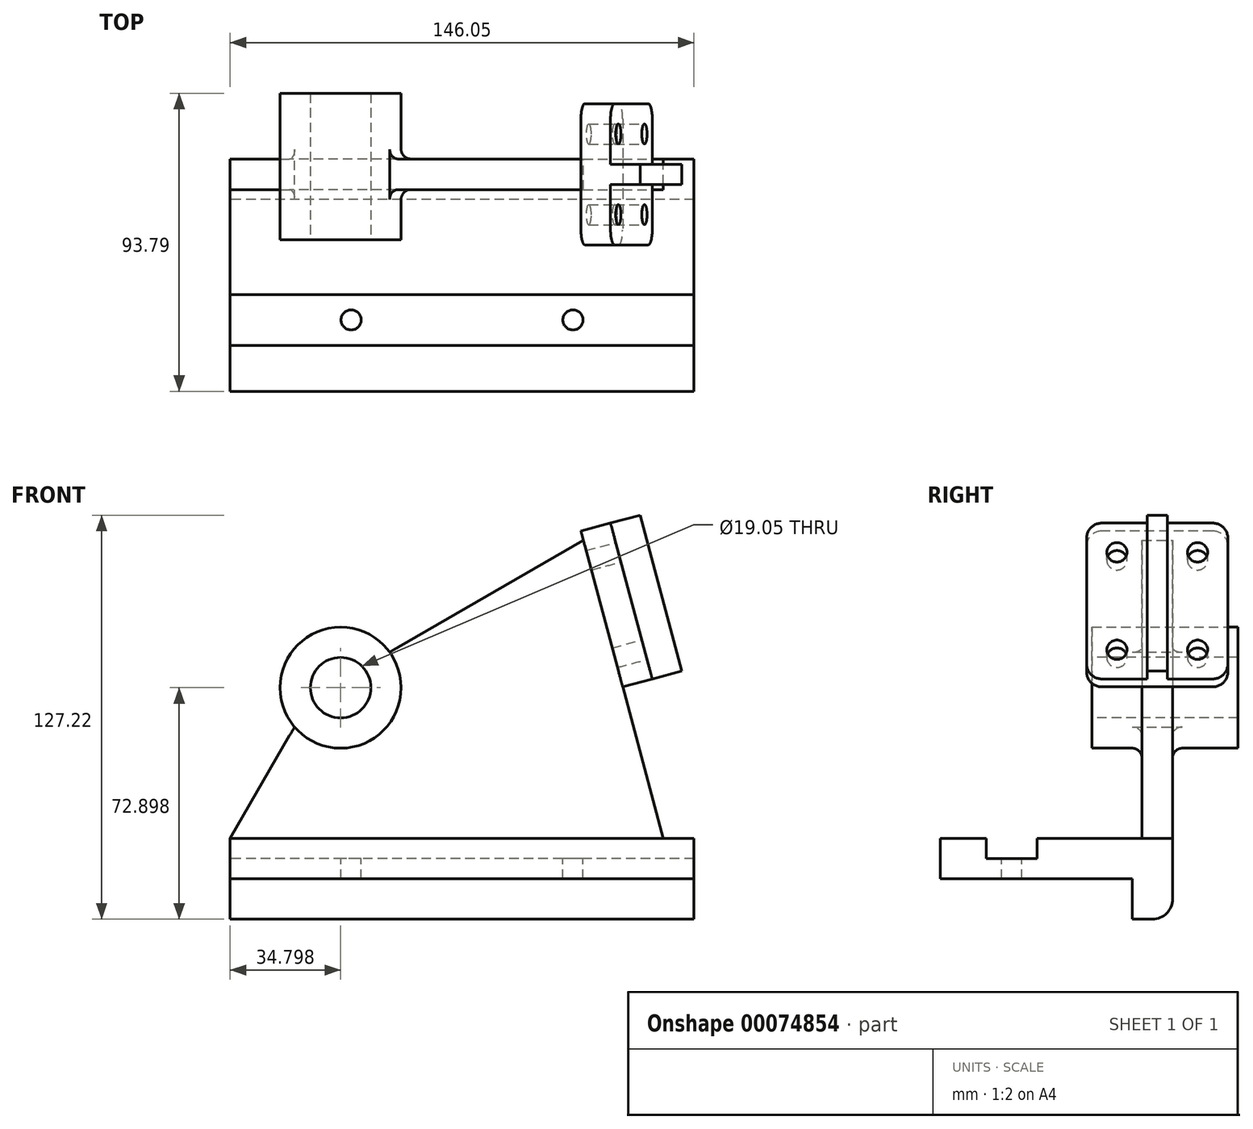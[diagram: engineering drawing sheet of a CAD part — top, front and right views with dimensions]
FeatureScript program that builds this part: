
annotation { "Feature Type Name" : "Feature", "Feature Type Description" : "" }
export const myFeature = defineFeature(function(context is Context, id is Id, definition is map)
    precondition{}
    {
        {
            var Q0;
            Q0=qCreatedBy(makeId("Right.planeOp"),FACE);
            var sketch = newSketch(context, id + "F0", { "sketchPlane" : qUnion([Q0])});
            skLineSegment(sketch, "E0", {"start": v(0, 0) * mm, "end": v(0, -25.4) * mm});
            skLineSegment(sketch, "E1", {"start": v(0, -25.4) * mm, "end": v(-12.7, -25.4) * mm});
            skLineSegment(sketch, "E2", {"start": v(-12.7, -25.4) * mm, "end": v(-12.7, -12.7) * mm});
            skLineSegment(sketch, "E3", {"start": v(-12.7, -12.7) * mm, "end": v(-73.15, -12.7) * mm});
            skLineSegment(sketch, "E4", {"start": v(-73.15, -12.7) * mm, "end": v(-73.15, 0) * mm});
            skLineSegment(sketch, "E5", {"start": v(-73.15, 0) * mm, "end": v(-58.67, 0) * mm});
            skLineSegment(sketch, "E6", {"start": v(-58.67, 0) * mm, "end": v(-58.67, -6.35) * mm});
            skLineSegment(sketch, "E7", {"start": v(-58.67, -6.35) * mm, "end": v(-42.67, -6.35) * mm});
            skLineSegment(sketch, "E8", {"start": v(-42.67, -6.35) * mm, "end": v(-42.67, 0) * mm});
            skLineSegment(sketch, "E9", {"start": v(-42.67, 0) * mm, "end": v(0, 0) * mm});
            skSolve(sketch);
        }
        {
            var Q0;
            Q0 = qSketchRegion(id + "F0", true);
            extrude(context, id + "F1", {"entities" : qUnion([Q0]), "depth" : 146.05 * mm});
        }
        {
            var Q0;
            Q0=makeQuery(id+"F1.opExtrude","SWEPT_FACE",FACE,{"disambiguationData":[OSD([sQuery(id+"F0.wireOp",EDGE,"E7")])]});
            var sketch = newSketch(context, id + "F2", { "sketchPlane" : qUnion([Q0])});
            skLineSegment(sketch, "E10", {"start": v(146.05, -50.67) * mm, "end": v(107.95, -50.67) * mm, "construction": true});
            skLineSegment(sketch, "E11", {"start": v(107.95, -50.67) * mm, "end": v(38.1, -50.67) * mm, "construction": true});
            skCircle(sketch, "E12", {"center": v(107.95, -50.67) * mm, "radius": 3.18 * mm});
            skCircle(sketch, "E13", {"center": v(38.1, -50.67) * mm, "radius": 3.18 * mm});
            skSolve(sketch);
        }
        {
            var Q0;
            Q0 = qSketchRegion(id + "F2", true);
            extrude(context, id + "F3", {"entities" : qUnion([Q0]), "operationType" : NewBodyOperationType.REMOVE, "endBound" : BoundingType.THROUGH_ALL, "oppositeDirection" : true, "depth" : 25.4 * mm});
        }
        {
            var Q0;
            Q0=makeQuery(id+"F1.opExtrude","SWEPT_EDGE",EDGE,{"disambiguationData":[OSD([sQuery(id+"F0.wireOp",EDGE,"E0"),sQuery(id+"F0.wireOp",EDGE,"E1")])]});
            fillet(context, id + "F4", {"entities" : qUnion([Q0]), "radius" : 6.35 * mm, "tangentPropagation" : true, "allowEdgeOverflow" : false});
        }
        {
            var Q0;
            Q0=makeQuery(id+"F1.opExtrude","SWEPT_FACE",FACE,{"disambiguationData":[OSD([sQuery(id+"F0.wireOp",EDGE,"E0")])]});
            var sketch = newSketch(context, id + "F5", { "sketchPlane" : qUnion([Q0])});
            skLineSegment(sketch, "E14", {"start": v(0, 0) * mm, "end": v(-34.8, 47.5) * mm, "construction": true});
            skLineSegment(sketch, "E15", {"start": v(-34.8, 47.5) * mm, "end": v(-50.23, 58.67) * mm});
            skLineSegment(sketch, "E16", {"start": v(-50.23, 58.67) * mm, "end": v(-111.24, 93.9) * mm});
            skLineSegment(sketch, "E17", {"start": v(-111.24, 93.9) * mm, "end": v(-136.4, 0) * mm});
            skLineSegment(sketch, "E18", {"start": v(-136.4, 0) * mm, "end": v(0, 0) * mm});
            skLineSegment(sketch, "E19", {"start": v(0, 0) * mm, "end": v(-20.3, 35.15) * mm});
            skCircle(sketch, "E20", {"center": v(-34.8, 47.5) * mm, "radius": 19.05 * mm, "construction": true});
            skLineSegment(sketch, "E21", {"start": v(0, 0) * mm, "end": v(0, 84.58) * mm, "construction": true});
            skLineSegment(sketch, "E22", {"start": v(-34.8, 47.5) * mm, "end": v(-34.8, 66.55) * mm, "construction": true});
            skLineSegment(sketch, "E23", {"start": v(-136.4, 0) * mm, "end": v(-136.4, 47.75) * mm, "construction": true});
            skLineSegment(sketch, "E24", {"start": v(-20.3, 35.15) * mm, "end": v(-34.8, 47.5) * mm});
            skLineSegment(sketch, "E25", {"start": v(-136.4, 47.75) * mm, "end": v(-123.6, 47.75) * mm, "construction": true});
            skSolve(sketch);
        }
        {
            var Q0;
            Q0 = qSketchRegion(id + "F5", true);
            extrude(context, id + "F6", {"entities" : qUnion([Q0]), "operationType" : NewBodyOperationType.ADD, "oppositeDirection" : true, "depth" : 9.65 * mm});
        }
        {
            var Q0;
            Q0=makeQuery(id+"F5.imprint","IMPRINT",FACE,{"disambiguationData":[TD([[makeQuery(id+"F5.imprint","IMPRINT",EDGE,{"derivedFrom":sQuery(id+"F5.wireOp",EDGE,"E15")}),1.0]])]});
            var sketch = newSketch(context, id + "F7", { "sketchPlane" : qUnion([Q0])});
            skCircle(sketch, "E26", {"center": v(-34.8, 47.5) * mm, "radius": 19.05 * mm});
            skSolve(sketch);
        }
        {
            var Q0;
            Q0 = qSketchRegion(id + "F7", true);
            extrude(context, id + "F8", {"entities" : qUnion([Q0]), "operationType" : NewBodyOperationType.ADD, "oppositeDirection" : true, "depth" : 25.4 * mm, "hasSecondDirection" : true, "secondDirectionOppositeDirection" : false, "secondDirectionDepth" : 20.64 * mm});
        }
        {
            var Q0;
            Q0=makeQuery(id+"F8.opExtrude","CAP_FACE",FACE,{"disambiguationData":[OSD([sQuery(id+"F7.wireOp",EDGE,"E26")])],"isStart":false});
            var sketch = newSketch(context, id + "F9", { "sketchPlane" : qUnion([Q0])});
            skCircle(sketch, "E27", {"center": v(34.8, 47.5) * mm, "radius": 9.53 * mm});
            skSolve(sketch);
        }
        {
            var Q0;
            Q0 = qSketchRegion(id + "F9", true);
            extrude(context, id + "F10", {"entities" : qUnion([Q0]), "operationType" : NewBodyOperationType.REMOVE, "endBound" : BoundingType.THROUGH_ALL, "oppositeDirection" : true, "depth" : 25.4 * mm});
        }
        {
            var Q0;
            Q0=makeQuery(id+"F6.opExtrude","SWEPT_FACE",FACE,{"disambiguationData":[OSD([sQuery(id+"F5.wireOp",EDGE,"E17")])]});
            var sketch = newSketch(context, id + "F11", { "sketchPlane" : qUnion([Q0])});
            skLineSegment(sketch, "E28", {"start": v(-4.83, 61.9) * mm, "end": v(-4.83, 39.53) * mm, "construction": true});
            skLineSegment(sketch, "E29.rect.bottom", {"start": v(17.4, 14.13) * mm, "end": v(-27.05, 14.13) * mm});
            skLineSegment(sketch, "E29.rect.top", {"start": v(17.4, 64.93) * mm, "end": v(-27.05, 64.93) * mm});
            skLineSegment(sketch, "E29.rect.left", {"start": v(17.4, 14.13) * mm, "end": v(17.4, 64.93) * mm});
            skLineSegment(sketch, "E29.rect.right", {"start": v(-27.05, 14.13) * mm, "end": v(-27.05, 64.93) * mm});
            skPoint(sketch, "E29.rect.middle", {"position": v(-4.83, 39.53) * mm});
            skSolve(sketch);
        }
        {
            var Q0;
            Q0 = qSketchRegion(id + "F11", true);
            extrude(context, id + "F12", {"entities" : qUnion([Q0]), "operationType" : NewBodyOperationType.ADD, "depth" : 9.65 * mm});
        }
        {
            var Q0;
            Q0=makeQuery(id+"F12.opExtrude","CAP_FACE",FACE,{"disambiguationData":[OSD([sQuery(id+"F11.wireOp",EDGE,"E29.rect.bottom"),sQuery(id+"F11.wireOp",EDGE,"E29.rect.top"),sQuery(id+"F11.wireOp",EDGE,"E29.rect.left"),sQuery(id+"F11.wireOp",EDGE,"E29.rect.right")])],"isStart":false});
            var sketch = newSketch(context, id + "F13", { "sketchPlane" : qUnion([Q0])});
            skLineSegment(sketch, "E30", {"start": v(-4.83, 64.93) * mm, "end": v(-4.83, 39.53) * mm, "construction": true});
            skPoint(sketch, "E30.endSnap0", {"position": v(17.4, 39.53) * mm});
            skLineSegment(sketch, "E31", {"start": v(-4.83, 39.53) * mm, "end": v(17.4, 39.53) * mm, "construction": true});
            skLineSegment(sketch, "E32.rect.bottom", {"start": v(7.87, 23.66) * mm, "end": v(-17.53, 23.66) * mm, "construction": true});
            skLineSegment(sketch, "E32.rect.top", {"start": v(7.87, 55.4) * mm, "end": v(-17.53, 55.4) * mm, "construction": true});
            skLineSegment(sketch, "E32.rect.left", {"start": v(7.87, 23.66) * mm, "end": v(7.87, 55.4) * mm, "construction": true});
            skLineSegment(sketch, "E32.rect.right", {"start": v(-17.53, 23.66) * mm, "end": v(-17.53, 55.4) * mm, "construction": true});
            skPoint(sketch, "E32.rect.middle", {"position": v(-4.83, 39.53) * mm});
            skCircle(sketch, "E33", {"center": v(-17.53, 55.4) * mm, "radius": 3.18 * mm});
            skCircle(sketch, "E34", {"center": v(7.87, 55.4) * mm, "radius": 3.18 * mm});
            skCircle(sketch, "E35", {"center": v(7.87, 23.66) * mm, "radius": 3.18 * mm});
            skCircle(sketch, "E36", {"center": v(-17.53, 23.66) * mm, "radius": 3.18 * mm});
            skSolve(sketch);
        }
        {
            var Q0;
            Q0 = qSketchRegion(id + "F13", true);
            extrude(context, id + "F14", {"entities" : qUnion([Q0]), "operationType" : NewBodyOperationType.REMOVE, "oppositeDirection" : true, "depth" : 9.65 * mm});
        }
        {
            var Q0;
            Q0=makeQuery(id+"F12.opExtrude","SWEPT_FACE",FACE,{"disambiguationData":[OSD([sQuery(id+"F11.wireOp",EDGE,"E29.rect.top")])]});
            var sketch = newSketch(context, id + "F15", { "sketchPlane" : qUnion([Q0])});
            skLineSegment(sketch, "E37.bottom", {"start": v(141.4, -8) * mm, "end": v(151.05, -8) * mm});
            skLineSegment(sketch, "E37.left", {"start": v(141.4, -8) * mm, "end": v(141.4, -1.65) * mm});
            skLineSegment(sketch, "E38", {"start": v(131.75, -4.83) * mm, "end": v(141.4, -4.83) * mm, "construction": true});
            skLineSegment(sketch, "E39", {"start": v(141.4, -1.65) * mm, "end": v(151.05, -1.65) * mm});
            skLineSegment(sketch, "E40", {"start": v(151.05, -1.65) * mm, "end": v(151.05, -8) * mm});
            skSolve(sketch);
        }
        {
            var Q0;
            Q0 = qSketchRegion(id + "F15", true);
            extrude(context, id + "F16", {"entities" : qUnion([Q0]), "operationType" : NewBodyOperationType.ADD, "oppositeDirection" : true, "depth" : 50.8 * mm});
        }
        {
            var Q0;
            Q0=makeQuery(id+"F12.opExtrude","SWEPT_EDGE",EDGE,{"disambiguationData":[OSD([sQuery(id+"F11.wireOp",EDGE,"E29.rect.top"),sQuery(id+"F11.wireOp",EDGE,"E29.rect.right")])]});
            var Q1;
            Q1=makeQuery(id+"F12.opExtrude","SWEPT_EDGE",EDGE,{"disambiguationData":[OSD([sQuery(id+"F11.wireOp",EDGE,"E29.rect.top"),sQuery(id+"F11.wireOp",EDGE,"E29.rect.left")])]});
            var Q2;
            Q2=makeQuery(id+"F12.opExtrude","SWEPT_EDGE",EDGE,{"disambiguationData":[OSD([sQuery(id+"F11.wireOp",EDGE,"E29.rect.bottom"),sQuery(id+"F11.wireOp",EDGE,"E29.rect.right")])]});
            var Q3;
            Q3=makeQuery(id+"F12.opExtrude","SWEPT_EDGE",EDGE,{"disambiguationData":[OSD([sQuery(id+"F11.wireOp",EDGE,"E29.rect.bottom"),sQuery(id+"F11.wireOp",EDGE,"E29.rect.left")])]});
            fillet(context, id + "F17", {"entities" : qUnion([Q0, Q1, Q2, Q3]), "radius" : 4.83 * mm, "tangentPropagation" : true, "allowEdgeOverflow" : false});
        }
        {
            var Q0;
            Q0=makeQuery(id+"F8.boolean.opBoolean","INTERSECT",EDGE,{"derivedFrom":[makeQuery(id+"F6.boolean.opBoolean","MERGE",FACE,{"derivedFrom":[makeQuery(id+"F1.opExtrude","SWEPT_FACE",FACE,{"disambiguationData":[OSD([sQuery(id+"F0.wireOp",EDGE,"E0")])]}),makeQuery(id+"F6.opExtrude","CAP_FACE",FACE,{"disambiguationData":[OSD([sQuery(id+"F5.wireOp",EDGE,"E15"),sQuery(id+"F5.wireOp",EDGE,"E16"),sQuery(id+"F5.wireOp",EDGE,"E17"),sQuery(id+"F5.wireOp",EDGE,"E18"),sQuery(id+"F5.wireOp",EDGE,"E19"),sQuery(id+"F5.wireOp",EDGE,"E24")])],"isStart":true})]}),makeQuery(id+"F8.opExtrude","SWEPT_FACE",FACE,{"disambiguationData":[OSD([sQuery(id+"F7.wireOp",EDGE,"E26")])]})]});
            var Q1;
            Q1=makeQuery(id+"F8.boolean.opBoolean","INTERSECT",EDGE,{"derivedFrom":[makeQuery(id+"F6.opExtrude","CAP_FACE",FACE,{"disambiguationData":[OSD([sQuery(id+"F5.wireOp",EDGE,"E15"),sQuery(id+"F5.wireOp",EDGE,"E16"),sQuery(id+"F5.wireOp",EDGE,"E17"),sQuery(id+"F5.wireOp",EDGE,"E18"),sQuery(id+"F5.wireOp",EDGE,"E19"),sQuery(id+"F5.wireOp",EDGE,"E24")])],"isStart":false}),makeQuery(id+"F8.opExtrude","SWEPT_FACE",FACE,{"disambiguationData":[OSD([sQuery(id+"F7.wireOp",EDGE,"E26")])]})]});
            var Q2;
            Q2=makeQuery(id+"F6.opExtrude","CAP_EDGE",EDGE,{"disambiguationData":[OSD([sQuery(id+"F5.wireOp",EDGE,"E18")])],"isStart":false});
            fillet(context, id + "F18", {"entities" : qUnion([Q0, Q1, Q2]), "radius" : 3.05 * mm, "tangentPropagation" : true, "allowEdgeOverflow" : false});
        }
    });
